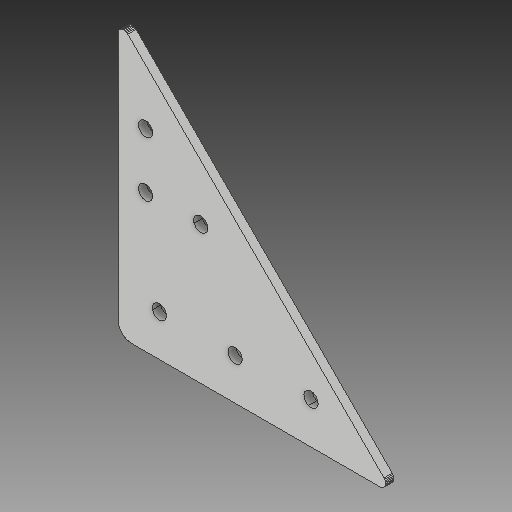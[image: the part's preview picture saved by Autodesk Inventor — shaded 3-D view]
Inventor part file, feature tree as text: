
AUTODESK INVENTOR PART (.ipt)
format: ipt  version: 2017 (Build 210142000, 142)  size: 230,400 bytes
history: native  units: mm
features: other x3, sketch x2, hole x1, projected_geometry x1
ambient origin geometry x8: Origin, YZ Plane, XZ Plane, XY Plane, X Axis, Y Axis, Z Axis, Center Point
bodies: Solid1 (feature_tree)
feature tree (7):
  other  "Side Brace.ipt"
  hole  "Hole1"  [1 undecoded]
  other  "Solid1::Side Brace.ipt"
  other  "TaggingFeature1"
  sketch  "Sketch1"  dims[d0=10.0mm]
  sketch  "Sketch2"  dims[d1=5.2mm d2=6.0mm d3=4.0mm d4=2.0mm d5=90.0deg d6=8.0mm d7=20.594885mm]
  projected_geometry  "Projected Loop1"
note: 1 required parameter value undecoded (feature->parameter linkage not recoverable at this tier; creation-order binding heuristic only, values carry confidence <= 0.55)
